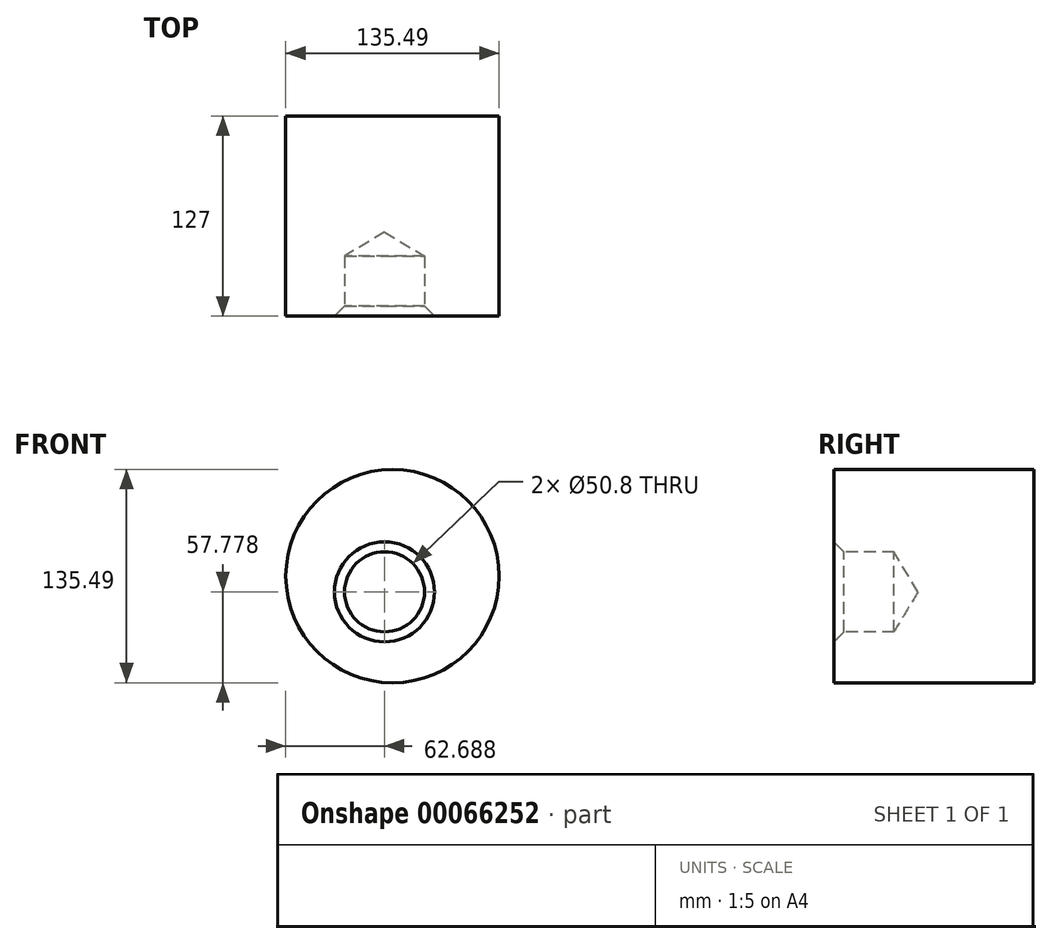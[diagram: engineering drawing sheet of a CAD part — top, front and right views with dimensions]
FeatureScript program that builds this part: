
annotation { "Feature Type Name" : "Feature", "Feature Type Description" : "" }
export const myFeature = defineFeature(function(context is Context, id is Id, definition is map)
    precondition{}
    {
        {
            var Q0;
            Q0=qCreatedBy(makeId("Front.planeOp"),FACE);
            var sketch = newSketch(context, id + "F0", { "sketchPlane" : qUnion([Q0])});
            skCircle(sketch, "E0", {"center": v(-21.8, -48.35) * mm, "radius": 67.74 * mm});
            skPoint(sketch, "E0.first.point", {"position": v(0, 15.78) * mm});
            skPoint(sketch, "E0.second.point", {"position": v(35, -11.46) * mm});
            skPoint(sketch, "E0.third.point", {"position": v(-31.09, 18.75) * mm});
            skSolve(sketch);
        }
        {
            var Q0;
            Q0=makeQuery(id+"F0.imprint","IMPRINT",FACE,{"disambiguationData":[TD([[makeQuery(id+"F0.imprint","IMPRINT",EDGE,{"derivedFrom":sQuery(id+"F0.wireOp",EDGE,"E0")}),1.0]])]});
            extrude(context, id + "F1", {"entities" : qUnion([Q0]), "depth" : 127 * mm});
        }
        {
            var Q0;
            Q0=makeQuery(id+"F1.opExtrude","CAP_FACE",FACE,{"disambiguationData":[OSD([sQuery(id+"F0.wireOp",EDGE,"E0")])],"isStart":false});
            var sketch = newSketch(context, id + "F2", { "sketchPlane" : qUnion([Q0])});
            skCircle(sketch, "E1", {"center": v(-26.86, -58.32) * mm, "radius": 26.47 * mm});
            skSolve(sketch);
        }
        {
            var Q0;
            Q0=sQuery(id+"F2.wireOp",VERTEX,"E1.center");
            var Q1;
            Q1=makeQuery(id+"F1.opExtrude","SWEPT_BODY",BODY,{"disambiguationData":[OSD([sQuery(id+"F0.wireOp",EDGE,"E0")])]});
            hole(context, id + "F3", {"style" : HoleStyle.C_SINK, "holeDiameter" : 50.8 * mm, "cSinkDiameter" : 63.5 * mm, "endStyle" : HoleEndStyle.BLIND, "holeDepth" : 38.1 * mm, "locations" : qUnion([Q0]), "scope" : qUnion([Q1]), "cSinkAngle" : 90 * degree});
        }
    });
